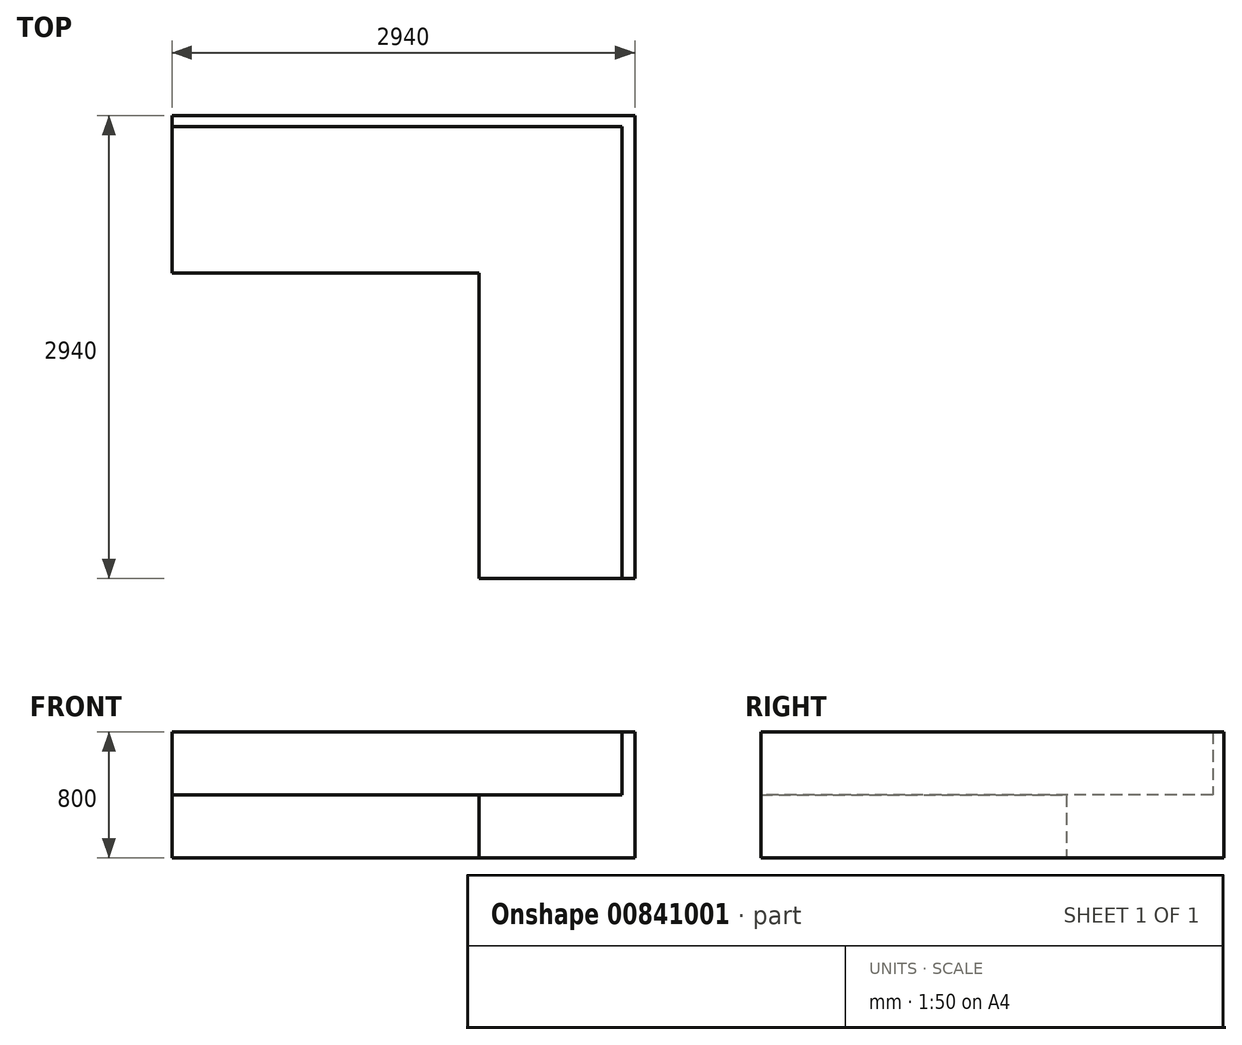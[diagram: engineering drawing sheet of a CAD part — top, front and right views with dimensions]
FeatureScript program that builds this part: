
annotation { "Feature Type Name" : "Feature", "Feature Type Description" : "" }
export const myFeature = defineFeature(function(context is Context, id is Id, definition is map)
    precondition{}
    {
        {
            var Q0;
            Q0=qCreatedBy(makeId("Top.planeOp"),FACE);
            var sketch = newSketch(context, id + "F0", { "sketchPlane" : qUnion([Q0])});
            skLineSegment(sketch, "E0.bottom", {"start": v(0, 0) * mm, "end": v(-2940, 0) * mm});
            skLineSegment(sketch, "E0.top", {"start": v(0, -1000) * mm, "end": v(-2940, -1000) * mm});
            skLineSegment(sketch, "E0.left", {"start": v(0, 0) * mm, "end": v(0, -1000) * mm});
            skLineSegment(sketch, "E0.right", {"start": v(-2940, 0) * mm, "end": v(-2940, -1000) * mm});
            skSolve(sketch);
        }
        {
            var Q0;
            Q0 = qSketchRegion(id + "F0", true);
            extrude(context, id + "F1", {"entities" : qUnion([Q0]), "depth" : 400 * mm, "offsetDistance" : 25 * mm});
        }
        {
            var Q0;
            Q0=makeQuery(id+"F1.opExtrude","SWEPT_FACE",FACE,{"disambiguationData":[OSD([sQuery(id+"F0.wireOp",EDGE,"E0.top")])]});
            var sketch = newSketch(context, id + "F2", { "sketchPlane" : qUnion([Q0])});
            skLineSegment(sketch, "E1.0", {"start": v(0, 400) * mm, "end": v(0, 0) * mm});
            skPoint(sketch, "E2", {"position": v(-952.93, 0) * mm});
            skPoint(sketch, "E3", {"position": v(0, 0) * mm});
            skLineSegment(sketch, "E4.bottom", {"start": v(0, 400) * mm, "end": v(-990, 400) * mm});
            skLineSegment(sketch, "E4.top", {"start": v(0, 0) * mm, "end": v(-990, 0) * mm});
            skLineSegment(sketch, "E4.right", {"start": v(-990, 400) * mm, "end": v(-990, 0) * mm});
            skSolve(sketch);
        }
        {
            var Q0;
            Q0=makeQuery(id+"F2.imprint","IMPRINT",FACE,{"disambiguationData":[TD([[makeQuery(id+"F2.imprint","IMPRINT",EDGE,{"derivedFrom":sQuery(id+"F2.wireOp",EDGE,"E4.bottom")}),1.0]])]});
            extrude(context, id + "F3", {"entities" : qUnion([Q0]), "operationType" : NewBodyOperationType.ADD, "depth" : 1940 * mm, "offsetDistance" : 25 * mm});
        }
        {
            var Q0;
            Q0=makeQuery(id+"F3.boolean.opBoolean","MERGE",FACE,{"derivedFrom":[makeQuery(id+"F1.opExtrude","CAP_FACE",FACE,{"disambiguationData":[OSD([sQuery(id+"F0.wireOp",EDGE,"E0.bottom"),sQuery(id+"F0.wireOp",EDGE,"E0.top"),sQuery(id+"F0.wireOp",EDGE,"E0.left"),sQuery(id+"F0.wireOp",EDGE,"E0.right")])],"isStart":false}),makeQuery(id+"F3.opExtrude","SWEPT_FACE",FACE,{"disambiguationData":[OSD([sQuery(id+"F2.wireOp",EDGE,"E4.bottom")])]})]});
            var sketch = newSketch(context, id + "F4", { "sketchPlane" : qUnion([Q0])});
            skLineSegment(sketch, "E5.bottom", {"start": v(-2940, -68.45) * mm, "end": v(0, -68.45) * mm});
            skLineSegment(sketch, "E5.top", {"start": v(-2940, 0) * mm, "end": v(0, 0) * mm});
            skLineSegment(sketch, "E5.left", {"start": v(-2940, -68.45) * mm, "end": v(-2940, 0) * mm});
            skLineSegment(sketch, "E5.right", {"start": v(0, -68.45) * mm, "end": v(0, 0) * mm});
            skLineSegment(sketch, "E6.bottom", {"start": v(-81.72, 0) * mm, "end": v(0, 0) * mm});
            skLineSegment(sketch, "E6.top", {"start": v(-81.72, -2940) * mm, "end": v(0, -2940) * mm});
            skLineSegment(sketch, "E6.left", {"start": v(-81.72, 0) * mm, "end": v(-81.72, -2940) * mm});
            skLineSegment(sketch, "E6.right", {"start": v(0, 0) * mm, "end": v(0, -2940) * mm});
            skPoint(sketch, "E7", {"position": v(-81.72, -68.45) * mm});
            skSolve(sketch);
        }
        {
            var Q0;
            {var subQ4=sQuery(id+"F4.wireOp",EDGE,"E5.top");Q0=makeQuery(id+"F4.imprint","IMPRINT",FACE,{"disambiguationData":[TD([[makeQuery(id+"F4.imprint","IMPRINT",EDGE,{"derivedFrom":subQ4}),1.0]])]});}
            var Q1;
            {var subQ5=sQuery(id+"F4.wireOp",EDGE,"E6.bottom");Q1=makeQuery(id+"F4.imprint","IMPRINT",FACE,{"disambiguationData":[TD([[makeQuery(id+"F4.imprint","IMPRINT",EDGE,{"derivedFrom":subQ5}),1.0]])]});}
            var Q2;
            {var subQ5=sQuery(id+"F4.wireOp",EDGE,"E6.top");Q2=makeQuery(id+"F4.imprint","IMPRINT",FACE,{"disambiguationData":[TD([[makeQuery(id+"F4.imprint","IMPRINT",EDGE,{"derivedFrom":subQ5}),-1.0]])]});}
            extrude(context, id + "F5", {"entities" : qUnion([Q0, Q1, Q2]), "operationType" : NewBodyOperationType.ADD, "depth" : 400 * mm, "offsetDistance" : 25 * mm});
        }
    });
